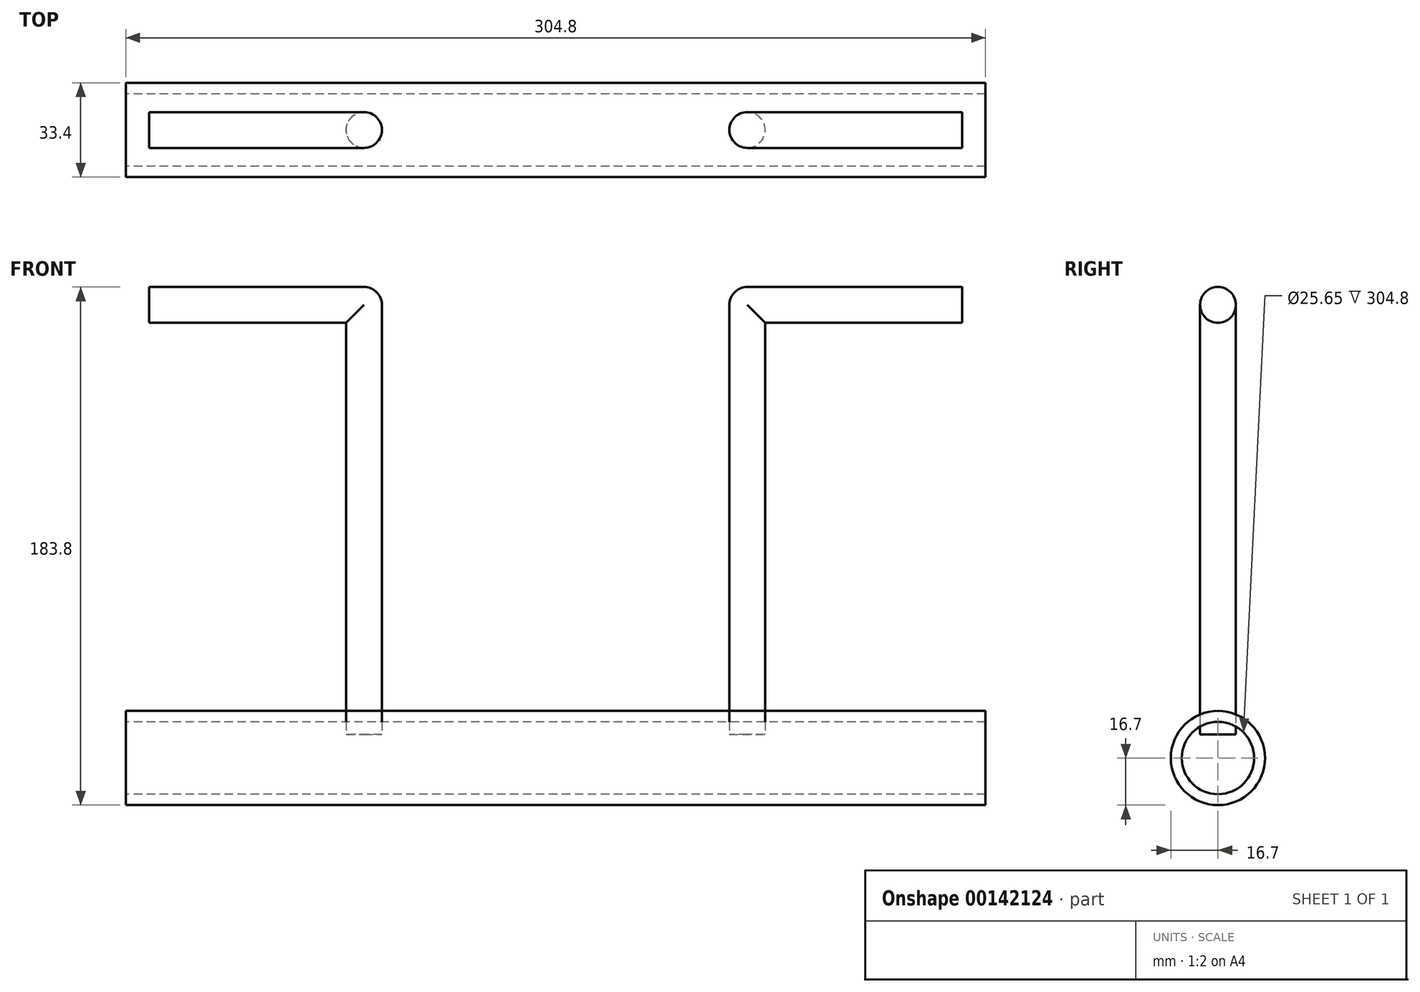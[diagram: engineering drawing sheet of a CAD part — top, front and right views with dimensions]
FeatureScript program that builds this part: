
annotation { "Feature Type Name" : "Feature", "Feature Type Description" : "" }
export const myFeature = defineFeature(function(context is Context, id is Id, definition is map)
    precondition{}
    {
        {
            var Q0;
            Q0=qCreatedBy(makeId("Front.planeOp"),FACE);
            var sketch = newSketch(context, id + "F0", { "sketchPlane" : qUnion([Q0])});
            skLineSegment(sketch, "E0.bottom", {"start": v(152.4, -8.35) * mm, "end": v(-152.4, -8.35) * mm});
            skLineSegment(sketch, "E0.top", {"start": v(152.4, 8.35) * mm, "end": v(-152.4, 8.35) * mm});
            skLineSegment(sketch, "E0.left", {"start": v(152.4, -8.35) * mm, "end": v(152.4, 8.35) * mm});
            skLineSegment(sketch, "E0.right", {"start": v(-152.4, -8.35) * mm, "end": v(-152.4, 8.35) * mm});
            skPoint(sketch, "E0.middle", {"position": v(0, 0) * mm});
            skSolve(sketch);
        }
        {
            var Q0;
            Q0 = qSketchRegion(id + "F0", true);
            var Q1;
            Q1=sQuery(id+"F0.wireOp",EDGE,"E0.bottom");
            revolve(context, id + "F1", {"entities" : qUnion([Q0]), "axis" : qUnion([Q1]), "revolveType" : RevolveType.FULL});
        }
        {
            var Q0;
            Q0=makeQuery(id+"F1.opRevolve","SWEPT_FACE",FACE,{"disambiguationData":[OSD([sQuery(id+"F0.wireOp",EDGE,"E0.right")])]});
            var sketch = newSketch(context, id + "F2", { "sketchPlane" : qUnion([Q0])});
            skCircle(sketch, "E1", {"center": v(0, -8.35) * mm, "radius": 12.83 * mm});
            skSolve(sketch);
        }
        {
            var Q0;
            Q0=qCreatedBy(makeId("Top.planeOp"),FACE);
            var sketch = newSketch(context, id + "F3", { "sketchPlane" : qUnion([Q0])});
            skCircle(sketch, "E2", {"center": v(-67.96, 0) * mm, "radius": 6.35 * mm});
            skSolve(sketch);
        }
        {
            var Q0;
            Q0 = qSketchRegion(id + "F2", true);
            extrude(context, id + "F4", {"entities" : qUnion([Q0]), "operationType" : NewBodyOperationType.REMOVE, "endBound" : BoundingType.THROUGH_ALL, "oppositeDirection" : true, "depth" : 25.4 * mm});
        }
        {
            var Q0;
            Q0 = qSketchRegion(id + "F3", true);
            extrude(context, id + "F5", {"entities" : qUnion([Q0]), "depth" : 152.4 * mm});
        }
        {
            var Q0;
            Q0=makeQuery(id+"F5.opExtrude","CAP_FACE",FACE,{"disambiguationData":[OSD([sQuery(id+"F3.wireOp",EDGE,"E2")])],"isStart":false});
            var sketch = newSketch(context, id + "F6", { "sketchPlane" : qUnion([Q0])});
            skLineSegment(sketch, "E3.bottom", {"start": v(-61.61, 0) * mm, "end": v(-67.96, 0) * mm});
            skLineSegment(sketch, "E3.top", {"start": v(-61.61, -6.35) * mm, "end": v(-67.96, -6.35) * mm});
            skLineSegment(sketch, "E3.left", {"start": v(-61.61, 0) * mm, "end": v(-61.61, -6.35) * mm});
            skLineSegment(sketch, "E3.right", {"start": v(-67.96, 0) * mm, "end": v(-67.96, -6.35) * mm});
            skSolve(sketch);
        }
        {
            var Q0;
            {var subQ0=sQuery(id+"F6.wireOp",EDGE,"E3.bottom");Q0=makeQuery(id+"F6.imprint","IMPRINT",FACE,{"disambiguationData":[TD([[makeQuery(id+"F6.imprint","IMPRINT",EDGE,{"derivedFrom":subQ0}),1.0]])]});}
            var Q1;
            Q1=sQuery(id+"F6.wireOp",EDGE,"E3.bottom");
            revolve(context, id + "F7", {"operationType" : NewBodyOperationType.ADD, "entities" : qUnion([Q0]), "axis" : qUnion([Q1]), "revolveType" : RevolveType.FULL});
        }
        {
            var Q0;
            Q0=makeQuery(id+"F7.opRevolve","SWEPT_FACE",FACE,{"disambiguationData":[OSD([sQuery(id+"F6.wireOp",EDGE,"E3.right")])]});
            var sketch = newSketch(context, id + "F8", { "sketchPlane" : qUnion([Q0])});
            skCircle(sketch, "E4", {"center": v(0, 152.4) * mm, "radius": 6.35 * mm});
            skSolve(sketch);
        }
        {
            var Q0;
            Q0 = qSketchRegion(id + "F8", true);
            extrude(context, id + "F9", {"entities" : qUnion([Q0]), "operationType" : NewBodyOperationType.ADD, "depth" : 76.2 * mm});
        }
        {
            var Q0;
            Q0=makeQuery(id+"F9.opExtrude","SWEPT_BODY",BODY,{"disambiguationData":[OSD([sQuery(id+"F8.wireOp",EDGE,"E4")])]});
            var Q1;
            Q1=makeQuery(id+"F5.opExtrude","SWEPT_BODY",BODY,{"disambiguationData":[OSD([sQuery(id+"F3.wireOp",EDGE,"E2")])]});
            var Q2;
            Q2=makeQuery(id+"F7.opRevolve","SWEPT_BODY",BODY,{"disambiguationData":[OSD([sQuery(id+"F3.wireOp",EDGE,"E2"),sQuery(id+"F6.wireOp",EDGE,"E3.bottom"),sQuery(id+"F6.wireOp",EDGE,"E3.right")])]});
            var Q3;
            Q3=qCreatedBy(makeId("Right.planeOp"),FACE);
            mirror(context, id + "F10", {"entities" : qUnion([Q0, Q1, Q2]), "mirrorPlane" : qUnion([Q3])});
        }
    });
